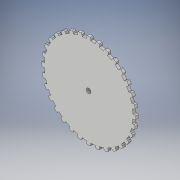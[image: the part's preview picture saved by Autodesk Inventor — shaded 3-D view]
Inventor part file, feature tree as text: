
AUTODESK INVENTOR PART (.ipt)
format: ipt  version: 2017 (Build 210142000, 142)  size: 341,504 bytes
history: native  units: in
note: dims shown in document units (in); Inventor stores cm internally (conversion verified against a paired STEP export)
features: extrude x2, sketch x2, pattern_circular x1
ambient origin geometry x8: Origin, YZ Plane, XZ Plane, XY Plane, X Axis, Y Axis, Z Axis, Center Point
bodies: Body1 (feature_tree)
feature tree (5):
  extrude  "Extrusion2"  Depth=0.075in
  pattern_circular  "Circular Pattern2"  Count=128 Angle=360.0deg
  extrude  "Extrusion3"  Depth=0.075in TaperAngle=0.0deg
  sketch  "Sketch1"  dims[d0=2.4in d10=0.075in]
  sketch  "Sketch2"  dims[d11=0.04in d12=50.3937in d14=360.0deg d16=0.075in d17=0.0in d18=12.5984in d19=360.0deg d21=0.126in d22=1.0in d23=0.0in]
